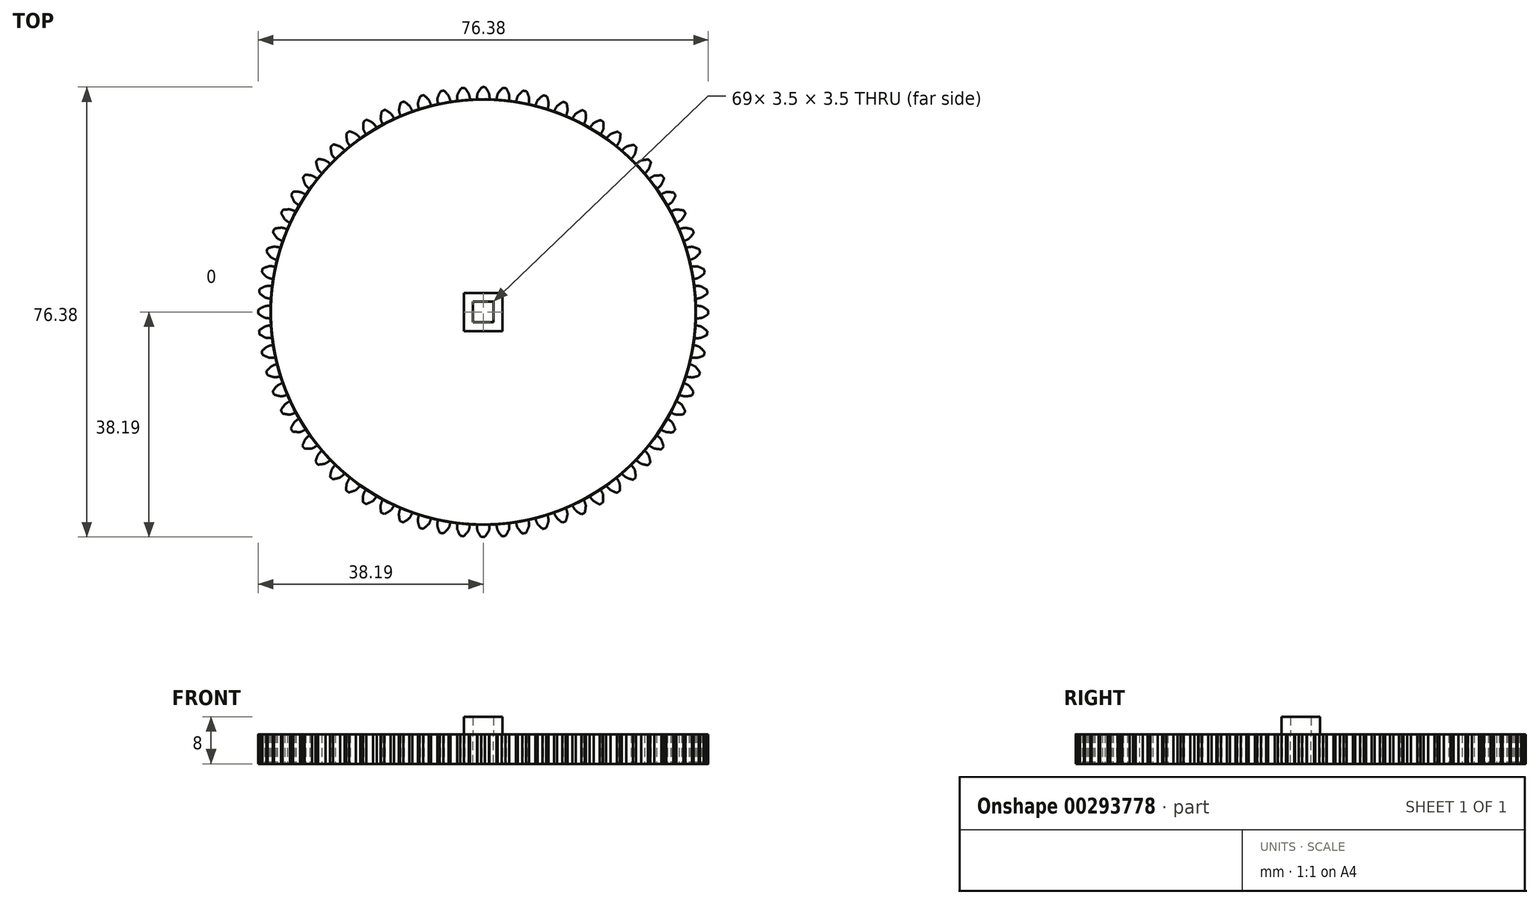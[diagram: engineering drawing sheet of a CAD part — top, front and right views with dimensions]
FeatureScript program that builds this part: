
annotation { "Feature Type Name" : "Feature", "Feature Type Description" : "" }
export const myFeature = defineFeature(function(context is Context, id is Id, definition is map)
    precondition{}
    {
        {
            var Q0;
            Q0=qCreatedBy(makeId("Top.planeOp"),FACE);
            var sketch = newSketch(context, id + "F0", { "sketchPlane" : qUnion([Q0])});
            skCircle(sketch, "E0", {"center": v(0, 0) * mm, "radius": 38.1 * mm, "construction": true});
            skCircle(sketch, "E1", {"center": v(0, 0) * mm, "radius": 36.1 * mm});
            skCircle(sketch, "E2", {"center": v(0, 0) * mm, "radius": 37.1 * mm, "construction": true});
            skLineSegment(sketch, "E3", {"start": v(0, 0) * mm, "end": v(0, 117.25) * mm, "construction": true});
            skLineSegment(sketch, "E4", {"start": v(0, 36.1) * mm, "end": v(-1, 36.1) * mm, "construction": true});
            skLineSegment(sketch, "E5", {"start": v(0, 36.1) * mm, "end": v(1, 36.1) * mm, "construction": true});
            skArc(sketch, "E6", {"start": v(1.08, 36.08) * mm, "mid": v(1.06, 36.62) * mm, "end": v(0.97, 37.14) * mm});
            skArc(sketch, "E7.trimOffspring", {"start": v(-0.96, 37.14) * mm, "mid": v(-1.05, 36.61) * mm, "end": v(-1.06, 36.08) * mm});
            skArc(sketch, "E8", {"start": v(0.97, 37.14) * mm, "mid": v(0.7, 37.67) * mm, "end": v(0.38, 38.17) * mm});
            skArc(sketch, "E9", {"start": v(0.38, 38.17) * mm, "mid": v(0.06, 38.19) * mm, "end": v(-0.25, 38.17) * mm});
            skArc(sketch, "E10.trimOffspring", {"start": v(-0.25, 38.17) * mm, "mid": v(-0.62, 37.67) * mm, "end": v(-0.96, 37.14) * mm});
            skSolve(sketch);
        }
        {
            var Q0;
            Q0 = qSketchRegion(id + "F0", true);
            extrude(context, id + "F1", {"entities" : qUnion([Q0]), "depth" : 5 * mm});
        }
        {
            var Q0;
            Q0=makeQuery(id+"F1.opExtrude","SWEPT_BODY",BODY,{"disambiguationData":[OSD([sQuery(id+"F0.wireOp",EDGE,"E1"),sQuery(id+"F0.wireOp",EDGE,"E6"),sQuery(id+"F0.wireOp",EDGE,"E7.trimOffspring"),sQuery(id+"F0.wireOp",EDGE,"E8"),sQuery(id+"F0.wireOp",EDGE,"E9"),sQuery(id+"F0.wireOp",EDGE,"E10.trimOffspring")])]});
            var Q1;
            Q1=makeQuery(id+"F1.opExtrude","SWEPT_FACE",FACE,{"disambiguationData":[OSD([sQuery(id+"F0.wireOp",EDGE,"E1")])]});
            circularPattern(context, id + "F2", {"entities" : qUnion([Q0]), "axis" : qUnion([Q1]), "angle" : 360 * degree, "instanceCount" : 68, "equalSpace" : true});
        }
        {
            var Q0;
            Q0=makeQuery(id+"F1.opExtrude","CAP_FACE",FACE,{"disambiguationData":[OSD([sQuery(id+"F0.wireOp",EDGE,"E1"),sQuery(id+"F0.wireOp",EDGE,"E6"),sQuery(id+"F0.wireOp",EDGE,"E7.trimOffspring"),sQuery(id+"F0.wireOp",EDGE,"E8"),sQuery(id+"F0.wireOp",EDGE,"E9"),sQuery(id+"F0.wireOp",EDGE,"E10.trimOffspring")])],"isStart":false});
            var sketch = newSketch(context, id + "F3", { "sketchPlane" : qUnion([Q0])});
            skLineSegment(sketch, "E11.bottom", {"start": v(1.75, -1.75) * mm, "end": v(-1.75, -1.75) * mm});
            skLineSegment(sketch, "E11.top", {"start": v(1.75, 1.75) * mm, "end": v(-1.75, 1.75) * mm});
            skLineSegment(sketch, "E11.left", {"start": v(1.75, -1.75) * mm, "end": v(1.75, 1.75) * mm});
            skLineSegment(sketch, "E11.right", {"start": v(-1.75, -1.75) * mm, "end": v(-1.75, 1.75) * mm});
            skPoint(sketch, "E11.middle", {"position": v(0, 0) * mm});
            skLineSegment(sketch, "E12.bottom", {"start": v(2.75, -2.75) * mm, "end": v(-2.75, -2.75) * mm});
            skLineSegment(sketch, "E12.top", {"start": v(2.75, 2.75) * mm, "end": v(-2.75, 2.75) * mm});
            skLineSegment(sketch, "E12.left", {"start": v(2.75, -2.75) * mm, "end": v(2.75, 2.75) * mm});
            skLineSegment(sketch, "E12.right", {"start": v(-2.75, -2.75) * mm, "end": v(-2.75, 2.75) * mm});
            skSolve(sketch);
        }
        {
            var Q0;
            Q0=makeQuery(id+"F3.imprint","IMPRINT",FACE,{"disambiguationData":[TD([[makeQuery(id+"F3.imprint","IMPRINT",EDGE,{"derivedFrom":sQuery(id+"F3.wireOp",EDGE,"E11.bottom")}),-1.0]])]});
            extrude(context, id + "F4", {"entities" : qUnion([Q0]), "operationType" : NewBodyOperationType.REMOVE, "oppositeDirection" : true, "depth" : 25 * mm});
        }
        {
            var Q0;
            Q0=makeQuery(id+"F2.opPattern","COPY",FACE,{"derivedFrom":makeQuery(id+"F1.opExtrude","CAP_FACE",FACE,{"disambiguationData":[OSD([sQuery(id+"F0.wireOp",EDGE,"E1"),sQuery(id+"F0.wireOp",EDGE,"E6"),sQuery(id+"F0.wireOp",EDGE,"E7.trimOffspring"),sQuery(id+"F0.wireOp",EDGE,"E8"),sQuery(id+"F0.wireOp",EDGE,"E9"),sQuery(id+"F0.wireOp",EDGE,"E10.trimOffspring")])],"isStart":false}),"instanceName":"7"});
            var sketch = newSketch(context, id + "F5", { "sketchPlane" : qUnion([Q0])});
            skLineSegment(sketch, "E13.bottom", {"start": v(-3.25, -3.25) * mm, "end": v(3.25, -3.25) * mm});
            skLineSegment(sketch, "E13.top", {"start": v(-3.25, 3.25) * mm, "end": v(3.25, 3.25) * mm});
            skLineSegment(sketch, "E13.left", {"start": v(-3.25, -3.25) * mm, "end": v(-3.25, 3.25) * mm});
            skLineSegment(sketch, "E13.right", {"start": v(3.25, -3.25) * mm, "end": v(3.25, 3.25) * mm});
            skPoint(sketch, "E13.middle", {"position": v(0, 0) * mm});
            skLineSegment(sketch, "E14.bottom", {"start": v(-1.75, -1.75) * mm, "end": v(1.75, -1.75) * mm});
            skLineSegment(sketch, "E14.top", {"start": v(-1.75, 1.75) * mm, "end": v(1.75, 1.75) * mm});
            skLineSegment(sketch, "E14.left", {"start": v(-1.75, -1.75) * mm, "end": v(-1.75, 1.75) * mm});
            skLineSegment(sketch, "E14.right", {"start": v(1.75, -1.75) * mm, "end": v(1.75, 1.75) * mm});
            skSolve(sketch);
        }
        {
            var Q0;
            Q0 = qSketchRegion(id + "F5", true);
            extrude(context, id + "F6", {"entities" : qUnion([Q0]), "depth" : 3 * mm});
        }
    });
